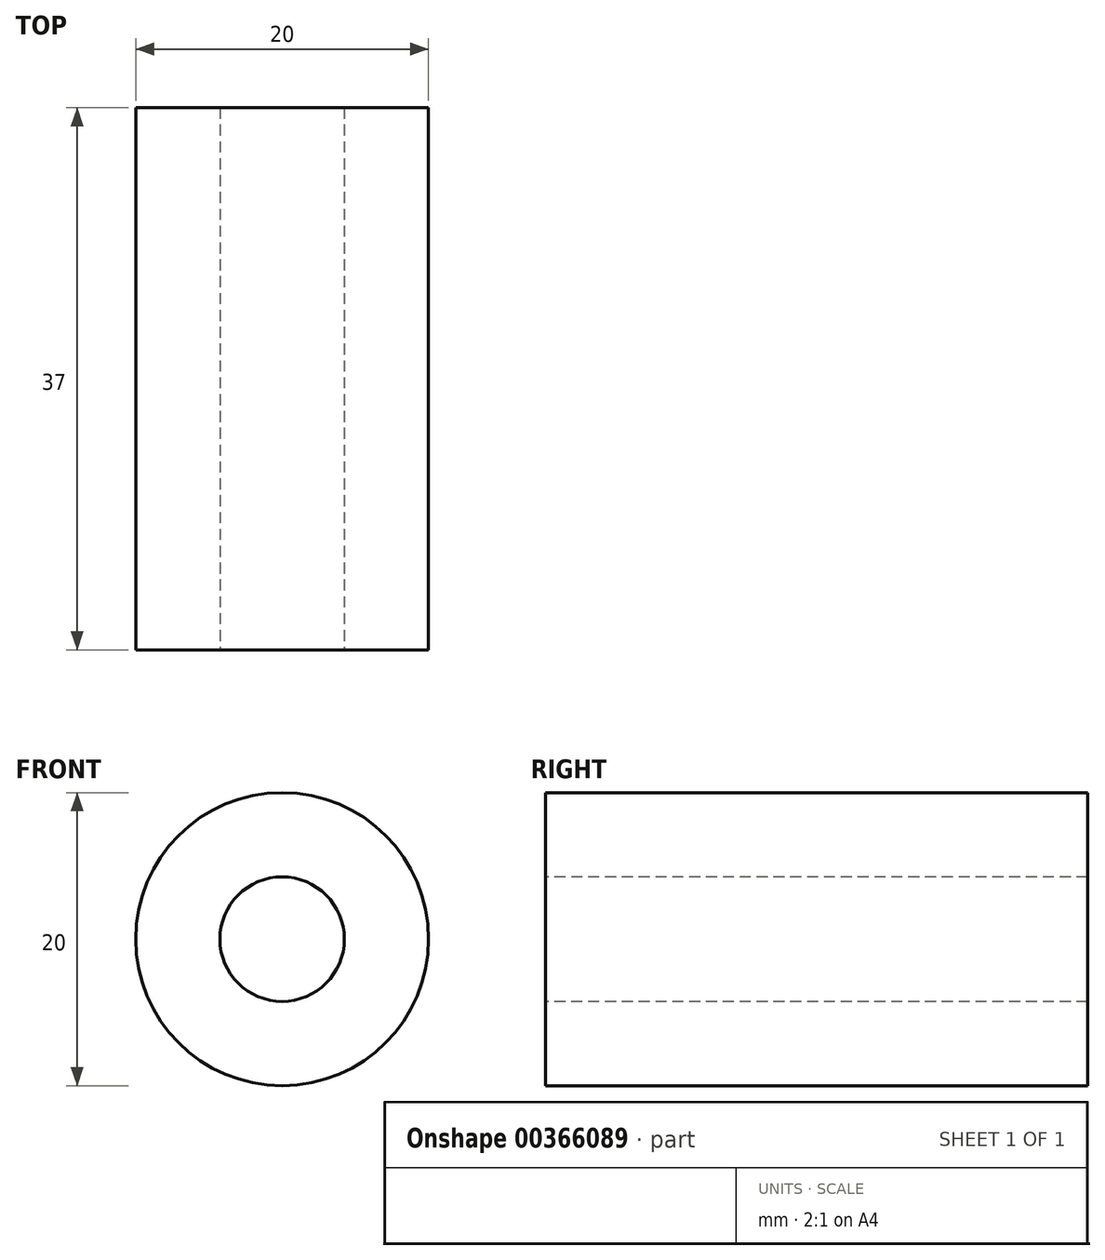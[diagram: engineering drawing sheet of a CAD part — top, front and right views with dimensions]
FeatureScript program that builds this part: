
annotation { "Feature Type Name" : "Feature", "Feature Type Description" : "" }
export const myFeature = defineFeature(function(context is Context, id is Id, definition is map)
    precondition{}
    {
        {
            var Q0;
            Q0=qCreatedBy(makeId("Front.planeOp"),FACE);
            var sketch = newSketch(context, id + "F0", { "sketchPlane" : qUnion([Q0])});
            skCircle(sketch, "E0", {"center": v(0, 0) * mm, "radius": 10 * mm});
            skSolve(sketch);
        }
        {
            var Q0;
            Q0 = qSketchRegion(id + "F0", true);
            extrude(context, id + "F1", {"entities" : qUnion([Q0]), "oppositeDirection" : true, "depth" : 37 * mm});
        }
        {
            var Q0;
            Q0=makeQuery(id+"F1.opExtrude","CAP_FACE",FACE,{"disambiguationData":[OSD([sQuery(id+"F0.wireOp",EDGE,"E0")])],"isStart":true});
            var sketch = newSketch(context, id + "F2", { "sketchPlane" : qUnion([Q0])});
            skCircle(sketch, "E1", {"center": v(0, 0) * mm, "radius": 4.25 * mm});
            skSolve(sketch);
        }
        {
            var Q0;
            Q0 = qSketchRegion(id + "F2", true);
            extrude(context, id + "F3", {"entities" : qUnion([Q0]), "operationType" : NewBodyOperationType.REMOVE, "endBound" : BoundingType.THROUGH_ALL, "oppositeDirection" : true, "depth" : 25 * mm});
        }
    });
